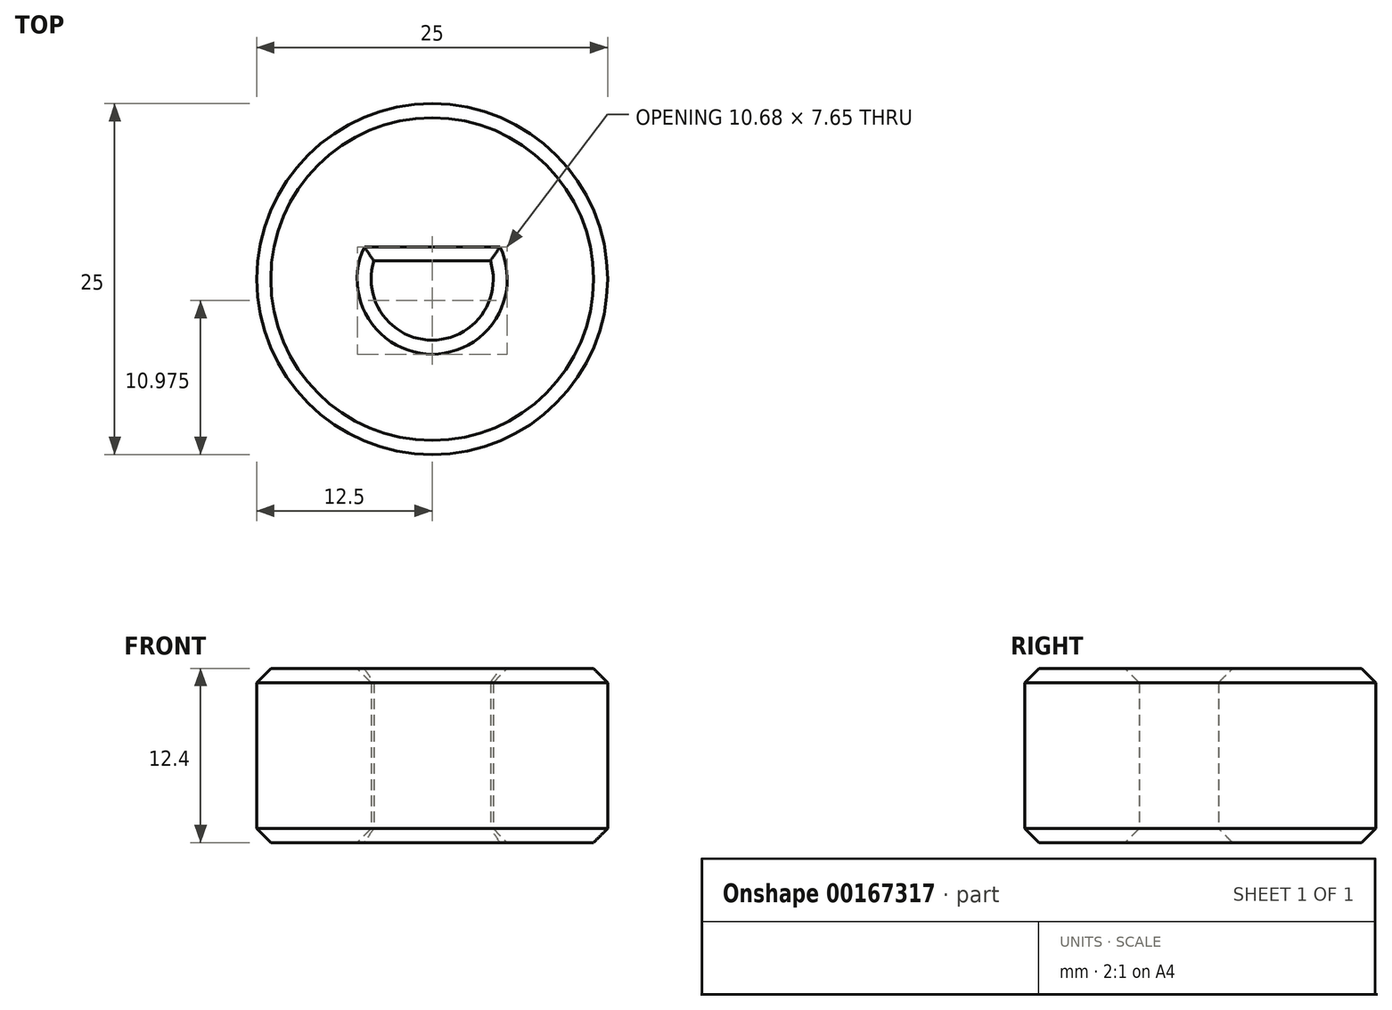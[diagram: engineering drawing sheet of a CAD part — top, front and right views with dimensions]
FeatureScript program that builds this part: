
annotation { "Feature Type Name" : "Feature", "Feature Type Description" : "" }
export const myFeature = defineFeature(function(context is Context, id is Id, definition is map)
    precondition{}
    {
        {
            var Q0;
            Q0=qCreatedBy(makeId("Top.planeOp"),FACE);
            var sketch = newSketch(context, id + "F0", { "sketchPlane" : qUnion([Q0])});
            skCircle(sketch, "E0", {"center": v(0, 0) * mm, "radius": 12.5 * mm});
            skCircle(sketch, "E1", {"center": v(0, 0) * mm, "radius": 4.35 * mm});
            skLineSegment(sketch, "E2.bottom", {"start": v(5, 1.3) * mm, "end": v(-5, 1.3) * mm});
            skLineSegment(sketch, "E2.top", {"start": v(5, -1.3) * mm, "end": v(-5, -1.3) * mm});
            skLineSegment(sketch, "E2.left", {"start": v(5, 1.3) * mm, "end": v(5, -1.3) * mm});
            skLineSegment(sketch, "E2.right", {"start": v(-5, 1.3) * mm, "end": v(-5, -1.3) * mm});
            skSolve(sketch);
        }
        {
            var Q0;
            Q0=makeQuery(id+"F0.imprint","IMPRINT",FACE,{"disambiguationData":[TD([[makeQuery(id+"F0.imprint","IMPRINT",EDGE,{"derivedFrom":sQuery(id+"F0.wireOp",EDGE,"E0")}),1.0]])]});
            var Q1;
            {var subQ5=sQuery(id+"F0.wireOp",EDGE,"E2.right");Q1=makeQuery(id+"F0.imprint","IMPRINT",FACE,{"disambiguationData":[TD([[makeQuery(id+"F0.imprint","IMPRINT",EDGE,{"derivedFrom":subQ5}),1.0]])]});}
            var Q2;
            {var subQ0=sQuery(id+"F0.wireOp",EDGE,"E2.bottom");var subQ1=sQuery(id+"F0.wireOp",EDGE,"E1");var subQ2=makeQuery(id+"F0.imprint","INTERSECT",VERTEX,{"disambiguationData":[OD(0.0)],"derivedFrom":[subQ1,subQ0]});Q2=makeQuery(id+"F0.imprint","IMPRINT",FACE,{"disambiguationData":[TD([[makeQuery(id+"F0.imprint","IMPRINT",EDGE,{"disambiguationData":[TD([[subQ2,-1.0]])],"derivedFrom":subQ1}),1.0]])]});}
            var Q3;
            {var subQ5=sQuery(id+"F0.wireOp",EDGE,"E2.left");Q3=makeQuery(id+"F0.imprint","IMPRINT",FACE,{"disambiguationData":[TD([[makeQuery(id+"F0.imprint","IMPRINT",EDGE,{"derivedFrom":subQ5}),-1.0]])]});}
            extrude(context, id + "F1", {"entities" : qUnion([Q0, Q1, Q2, Q3]), "depth" : 12.4 * mm});
        }
        {
            var Q0;
            Q0=makeQuery(id+"F1.opExtrude","CAP_EDGE",EDGE,{"disambiguationData":[OSD([sQuery(id+"F0.wireOp",EDGE,"E0")])],"isStart":false});
            var Q1;
            {var subQ0=sQuery(id+"F0.wireOp",EDGE,"E2.top");var subQ1=sQuery(id+"F0.wireOp",EDGE,"E1");Q1=makeQuery(id+"F1.opExtrude","CAP_EDGE",EDGE,{"disambiguationData":[OSD([subQ1]),TDD([makeQuery(id+"F0.imprint","IMPRINT",EDGE,{"disambiguationData":[TD([[makeQuery(id+"F0.imprint","INTERSECT",VERTEX,{"disambiguationData":[OD(0.0)],"derivedFrom":[subQ1,subQ0]}),-1.0]])],"derivedFrom":subQ1})])],"isStart":false});}
            var Q2;
            Q2=makeQuery(id+"F1.opExtrude","CAP_EDGE",EDGE,{"disambiguationData":[OSD([sQuery(id+"F0.wireOp",EDGE,"E2.top")])],"isStart":false});
            var Q3;
            Q3=makeQuery(id+"F1.opExtrude","CAP_EDGE",EDGE,{"disambiguationData":[OSD([sQuery(id+"F0.wireOp",EDGE,"E2.bottom")])],"isStart":false});
            var Q4;
            {var subQ0=sQuery(id+"F0.wireOp",EDGE,"E2.bottom");var subQ1=sQuery(id+"F0.wireOp",EDGE,"E1");Q4=makeQuery(id+"F1.opExtrude","CAP_EDGE",EDGE,{"disambiguationData":[OSD([subQ1]),TDD([makeQuery(id+"F0.imprint","IMPRINT",EDGE,{"disambiguationData":[TD([[makeQuery(id+"F0.imprint","INTERSECT",VERTEX,{"disambiguationData":[OD(0.0)],"derivedFrom":[subQ1,subQ0]}),1.0]])],"derivedFrom":subQ1})])],"isStart":false});}
            var Q5;
            Q5=makeQuery(id+"F1.opExtrude","CAP_EDGE",EDGE,{"disambiguationData":[OSD([sQuery(id+"F0.wireOp",EDGE,"E0")])],"isStart":true});
            var Q6;
            Q6=makeQuery(id+"F1.opExtrude","CAP_EDGE",EDGE,{"disambiguationData":[OSD([sQuery(id+"F0.wireOp",EDGE,"E2.bottom")])],"isStart":true});
            var Q7;
            {var subQ0=sQuery(id+"F0.wireOp",EDGE,"E2.bottom");var subQ1=sQuery(id+"F0.wireOp",EDGE,"E1");Q7=makeQuery(id+"F1.opExtrude","CAP_EDGE",EDGE,{"disambiguationData":[OSD([subQ1]),TDD([makeQuery(id+"F0.imprint","IMPRINT",EDGE,{"disambiguationData":[TD([[makeQuery(id+"F0.imprint","INTERSECT",VERTEX,{"disambiguationData":[OD(0.0)],"derivedFrom":[subQ1,subQ0]}),1.0]])],"derivedFrom":subQ1})])],"isStart":true});}
            var Q8;
            Q8=makeQuery(id+"F1.opExtrude","CAP_EDGE",EDGE,{"disambiguationData":[OSD([sQuery(id+"F0.wireOp",EDGE,"E2.top")])],"isStart":true});
            var Q9;
            {var subQ0=sQuery(id+"F0.wireOp",EDGE,"E2.top");var subQ1=sQuery(id+"F0.wireOp",EDGE,"E1");Q9=makeQuery(id+"F1.opExtrude","CAP_EDGE",EDGE,{"disambiguationData":[OSD([subQ1]),TDD([makeQuery(id+"F0.imprint","IMPRINT",EDGE,{"disambiguationData":[TD([[makeQuery(id+"F0.imprint","INTERSECT",VERTEX,{"disambiguationData":[OD(0.0)],"derivedFrom":[subQ1,subQ0]}),-1.0]])],"derivedFrom":subQ1})])],"isStart":true});}
            chamfer(context, id + "F2", {"entities" : qUnion([Q0, Q1, Q2, Q3, Q4, Q5, Q6, Q7, Q8, Q9]), "width" : 1 * mm, "tangentPropagation" : true});
        }
    });
